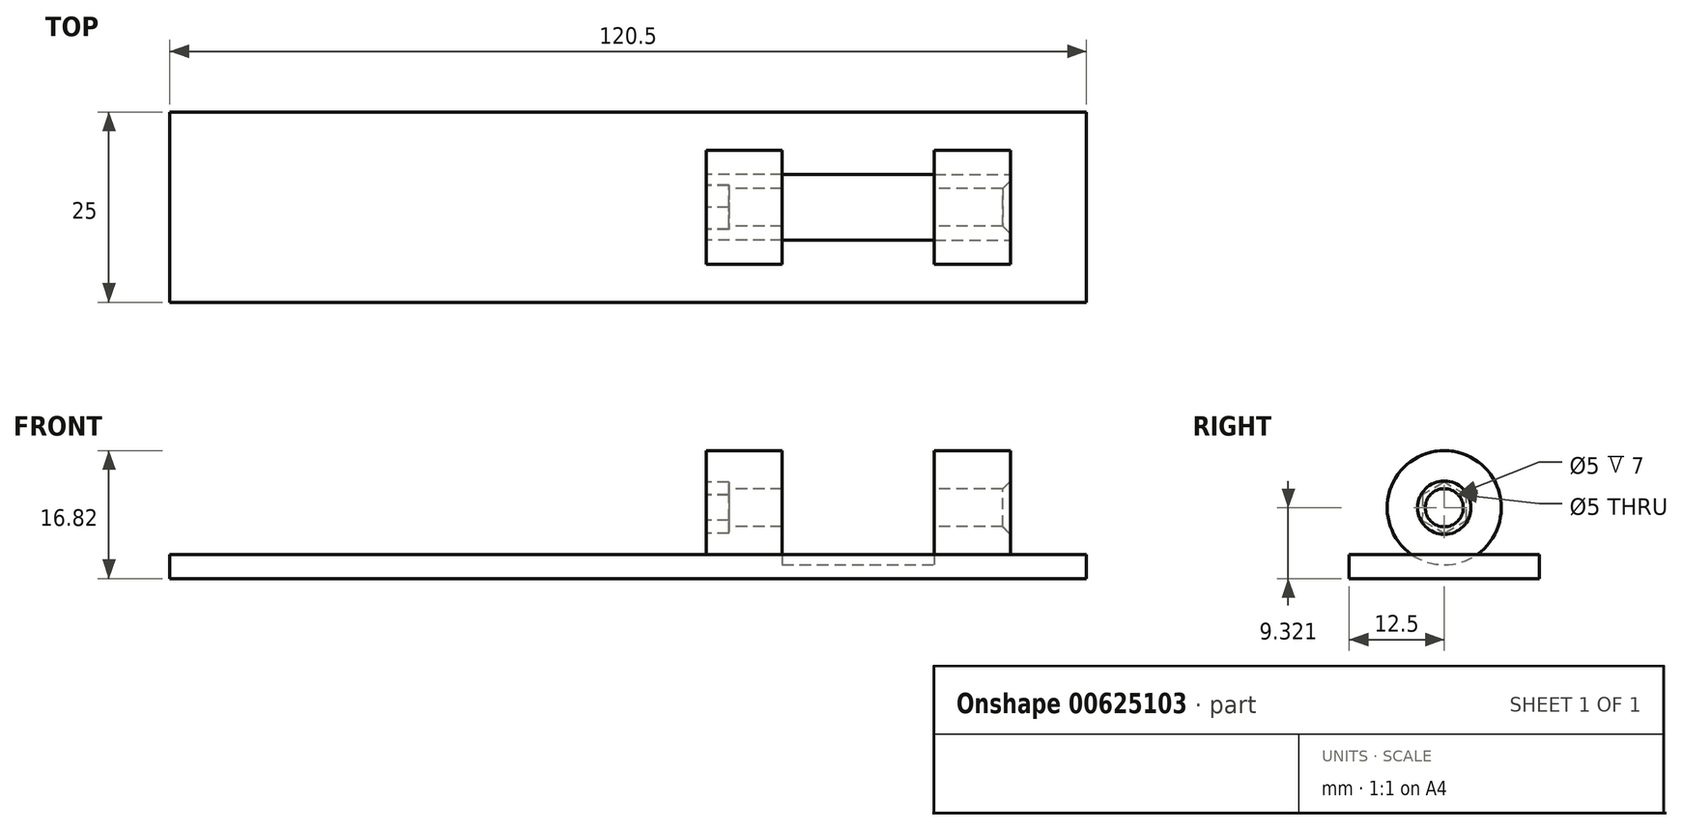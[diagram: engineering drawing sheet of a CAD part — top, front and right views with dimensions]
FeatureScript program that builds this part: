
annotation { "Feature Type Name" : "Feature", "Feature Type Description" : "" }
export const myFeature = defineFeature(function(context is Context, id is Id, definition is map)
    precondition{}
    {
        {
            var Q0;
            Q0=qCreatedBy(makeId("Front.planeOp"),FACE);
            var sketch = newSketch(context, id + "F0", { "sketchPlane" : qUnion([Q0])});
            skLineSegment(sketch, "E0.bottom", {"start": v(60.25, -1.59) * mm, "end": v(-60.25, -1.59) * mm});
            skLineSegment(sketch, "E0.top", {"start": v(60.25, 1.59) * mm, "end": v(-60.25, 1.59) * mm});
            skLineSegment(sketch, "E0.left", {"start": v(60.25, -1.59) * mm, "end": v(60.25, 1.59) * mm});
            skLineSegment(sketch, "E0.right", {"start": v(-60.25, -1.59) * mm, "end": v(-60.25, 1.59) * mm});
            skPoint(sketch, "E0.middle", {"position": v(0, 0) * mm});
            skSolve(sketch);
        }
        {
            var Q0;
            Q0 = qSketchRegion(id + "F0", true);
            extrude(context, id + "F1", {"entities" : qUnion([Q0]), "depth" : 25 * mm, "offsetDistance" : 25 * mm});
        }
        {
            var Q0;
            Q0=makeQuery(id+"F1.opExtrude","SWEPT_FACE",FACE,{"disambiguationData":[OSD([sQuery(id+"F0.wireOp",EDGE,"E0.left")])]});
            var sketch = newSketch(context, id + "F2", { "sketchPlane" : qUnion([Q0])});
            skCircle(sketch, "E1", {"center": v(-12.5, 7.73) * mm, "radius": 7.5 * mm});
            skPoint(sketch, "E1.centerSnap0", {"position": v(-12.5, 1.59) * mm});
            skSolve(sketch);
        }
        {
            var Q0;
            Q0 = qSketchRegion(id + "F2", true);
            var Q1;
            Q1 = qSketchRegion(id + "FFFjkV45fjTUnMO_1", true);
            extrude(context, id + "F3", {"entities" : qUnion([Q0, Q1]), "operationType" : NewBodyOperationType.ADD, "oppositeDirection" : true, "depth" : 20 * mm, "offsetDistance" : 25 * mm});
        }
        {
            var Q0;
            Q0=makeQuery(id+"F3.opExtrude","CAP_FACE",FACE,{"disambiguationData":[OSD([sQuery(id+"F2.wireOp",EDGE,"E1")])],"isStart":false});
            var sketch = newSketch(context, id + "F4", { "sketchPlane" : qUnion([Q0])});
            skCircle(sketch, "E2", {"center": v(12.5, 7.73) * mm, "radius": 7.5 * mm});
            skSolve(sketch);
        }
        {
            var Q0;
            Q0 = qSketchRegion(id + "F4", true);
            extrude(context, id + "F5", {"entities" : qUnion([Q0]), "operationType" : NewBodyOperationType.REMOVE, "depth" : 20 * mm, "offsetDistance" : 25 * mm});
        }
        {
            var Q0;
            Q0=makeQuery(id+"F1.opExtrude","SWEPT_FACE",FACE,{"disambiguationData":[OSD([sQuery(id+"F0.wireOp",EDGE,"E0.right")])]});
            var sketch = newSketch(context, id + "F6", { "sketchPlane" : qUnion([Q0])});
            skCircle(sketch, "E3", {"center": v(12.5, 7.73) * mm, "radius": 7.5 * mm});
            skPoint(sketch, "E3.centerSnap0", {"position": v(12.5, 1.59) * mm});
            skSolve(sketch);
        }
        {
            var Q0;
            Q0 = qSketchRegion(id + "F6", true);
            extrude(context, id + "F7", {"entities" : qUnion([Q0]), "operationType" : NewBodyOperationType.ADD, "oppositeDirection" : true, "depth" : 80.5 * mm, "offsetDistance" : 25 * mm});
        }
        {
            var Q0;
            Q0=makeQuery(id+"F7.boolean.opBoolean","MERGE",FACE,{"derivedFrom":[makeQuery(id+"F1.opExtrude","SWEPT_FACE",FACE,{"disambiguationData":[OSD([sQuery(id+"F0.wireOp",EDGE,"E0.right")])]}),makeQuery(id+"F7.opExtrude","CAP_FACE",FACE,{"disambiguationData":[OSD([sQuery(id+"F6.wireOp",EDGE,"E3")])],"isStart":true})]});
            var sketch = newSketch(context, id + "F8", { "sketchPlane" : qUnion([Q0])});
            skLineSegment(sketch, "E4.bottom", {"start": v(0, 1.59) * mm, "end": v(26.14, 1.59) * mm});
            skLineSegment(sketch, "E4.top", {"start": v(0, 15.7) * mm, "end": v(26.14, 15.7) * mm});
            skLineSegment(sketch, "E4.left", {"start": v(0, 1.59) * mm, "end": v(0, 15.7) * mm});
            skLineSegment(sketch, "E4.right", {"start": v(26.14, 1.59) * mm, "end": v(26.14, 15.7) * mm});
            skSolve(sketch);
        }
        {
            var Q0;
            Q0 = qSketchRegion(id + "F8", true);
            extrude(context, id + "F9", {"entities" : qUnion([Q0]), "operationType" : NewBodyOperationType.REMOVE, "oppositeDirection" : true, "depth" : 70.5 * mm, "offsetDistance" : 25 * mm});
        }
        {
            var Q0;
            Q0=makeQuery(id+"F3.boolean.opBoolean","MERGE",FACE,{"derivedFrom":[makeQuery(id+"F1.opExtrude","SWEPT_FACE",FACE,{"disambiguationData":[OSD([sQuery(id+"F0.wireOp",EDGE,"E0.left")])]}),makeQuery(id+"F3.opExtrude","CAP_FACE",FACE,{"disambiguationData":[OSD([sQuery(id+"F2.wireOp",EDGE,"E1")])],"isStart":true})]});
            var sketch = newSketch(context, id + "F10", { "sketchPlane" : qUnion([Q0])});
            skLineSegment(sketch, "E5.bottom", {"start": v(-25, 1.59) * mm, "end": v(0, 1.59) * mm});
            skLineSegment(sketch, "E5.top", {"start": v(-25, 16.45) * mm, "end": v(0, 16.45) * mm});
            skLineSegment(sketch, "E5.left", {"start": v(-25, 1.59) * mm, "end": v(-25, 16.45) * mm});
            skLineSegment(sketch, "E5.right", {"start": v(0, 1.59) * mm, "end": v(0, 16.45) * mm});
            skSolve(sketch);
        }
        {
            var Q0;
            Q0 = qSketchRegion(id + "F10", true);
            extrude(context, id + "F11", {"entities" : qUnion([Q0]), "operationType" : NewBodyOperationType.REMOVE, "oppositeDirection" : true, "depth" : 10 * mm, "offsetDistance" : 25 * mm});
        }
        {
            var Q0;
            Q0=makeQuery(id+"F9.boolean.opBoolean","COPY",FACE,{"derivedFrom":makeQuery(id+"F9.opExtrude","CAP_FACE",FACE,{"disambiguationData":[OSD([sQuery(id+"F8.wireOp",EDGE,"E4.bottom"),sQuery(id+"F8.wireOp",EDGE,"E4.top"),sQuery(id+"F8.wireOp",EDGE,"E4.left"),sQuery(id+"F8.wireOp",EDGE,"E4.right")])],"isStart":false})});
            var sketch = newSketch(context, id + "F12", { "sketchPlane" : qUnion([Q0])});
            skCircle(sketch, "E6", {"center": v(12.5, 7.73) * mm, "radius": 2.5 * mm});
            skSolve(sketch);
        }
        {
            var Q0;
            Q0 = qSketchRegion(id + "F12", true);
            extrude(context, id + "F13", {"entities" : qUnion([Q0]), "operationType" : NewBodyOperationType.REMOVE, "oppositeDirection" : true, "depth" : 80 * mm, "offsetDistance" : 25 * mm});
        }
        {
            var Q0;
            Q0=makeQuery(id+"F9.boolean.opBoolean","COPY",FACE,{"derivedFrom":makeQuery(id+"F9.opExtrude","CAP_FACE",FACE,{"disambiguationData":[OSD([sQuery(id+"F8.wireOp",EDGE,"E4.bottom"),sQuery(id+"F8.wireOp",EDGE,"E4.top"),sQuery(id+"F8.wireOp",EDGE,"E4.left"),sQuery(id+"F8.wireOp",EDGE,"E4.right")])],"isStart":false})});
            var sketch = newSketch(context, id + "F14", { "sketchPlane" : qUnion([Q0])});
            skCircle(sketch, "E7.cCircle", {"center": v(12.5, 7.73) * mm, "radius": 2.9 * mm, "construction": true});
            skLineSegment(sketch, "E7.0", {"start": v(15.4, 6.07) * mm, "end": v(12.51, 4.4) * mm});
            skLineSegment(sketch, "E7.1", {"start": v(12.51, 4.4) * mm, "end": v(9.61, 6.05) * mm});
            skLineSegment(sketch, "E7.2", {"start": v(9.61, 6.05) * mm, "end": v(9.6, 9.39) * mm});
            skLineSegment(sketch, "E7.3", {"start": v(9.6, 9.39) * mm, "end": v(12.49, 11.07) * mm});
            skLineSegment(sketch, "E7.4", {"start": v(12.49, 11.07) * mm, "end": v(15.39, 9.41) * mm});
            skLineSegment(sketch, "E7.5", {"start": v(15.39, 9.41) * mm, "end": v(15.4, 6.07) * mm});
            skPoint(sketch, "E7.0.midPoint", {"position": v(13.96, 5.23) * mm});
            skSolve(sketch);
        }
        {
            var Q0;
            Q0 = qSketchRegion(id + "F14", true);
            extrude(context, id + "F15", {"entities" : qUnion([Q0]), "operationType" : NewBodyOperationType.REMOVE, "oppositeDirection" : true, "depth" : 3 * mm, "offsetDistance" : 25 * mm});
        }
        {
            var Q0;
            Q0=makeQuery(id+"F13.boolean.opBoolean","INTERSECT",EDGE,{"derivedFrom":[makeQuery(id+"F11.boolean.opBoolean","COPY",FACE,{"derivedFrom":makeQuery(id+"F11.opExtrude","CAP_FACE",FACE,{"disambiguationData":[OSD([sQuery(id+"F10.wireOp",EDGE,"E5.bottom"),sQuery(id+"F10.wireOp",EDGE,"E5.top"),sQuery(id+"F10.wireOp",EDGE,"E5.left"),sQuery(id+"F10.wireOp",EDGE,"E5.right")])],"isStart":false})}),makeQuery(id+"F13.opExtrude","SWEPT_FACE",FACE,{"disambiguationData":[OSD([sQuery(id+"F12.wireOp",EDGE,"E6")])]})]});
            chamfer(context, id + "F16", {"entities" : qUnion([Q0]), "width" : 1 * mm, "tangentPropagation" : true});
        }
    });
